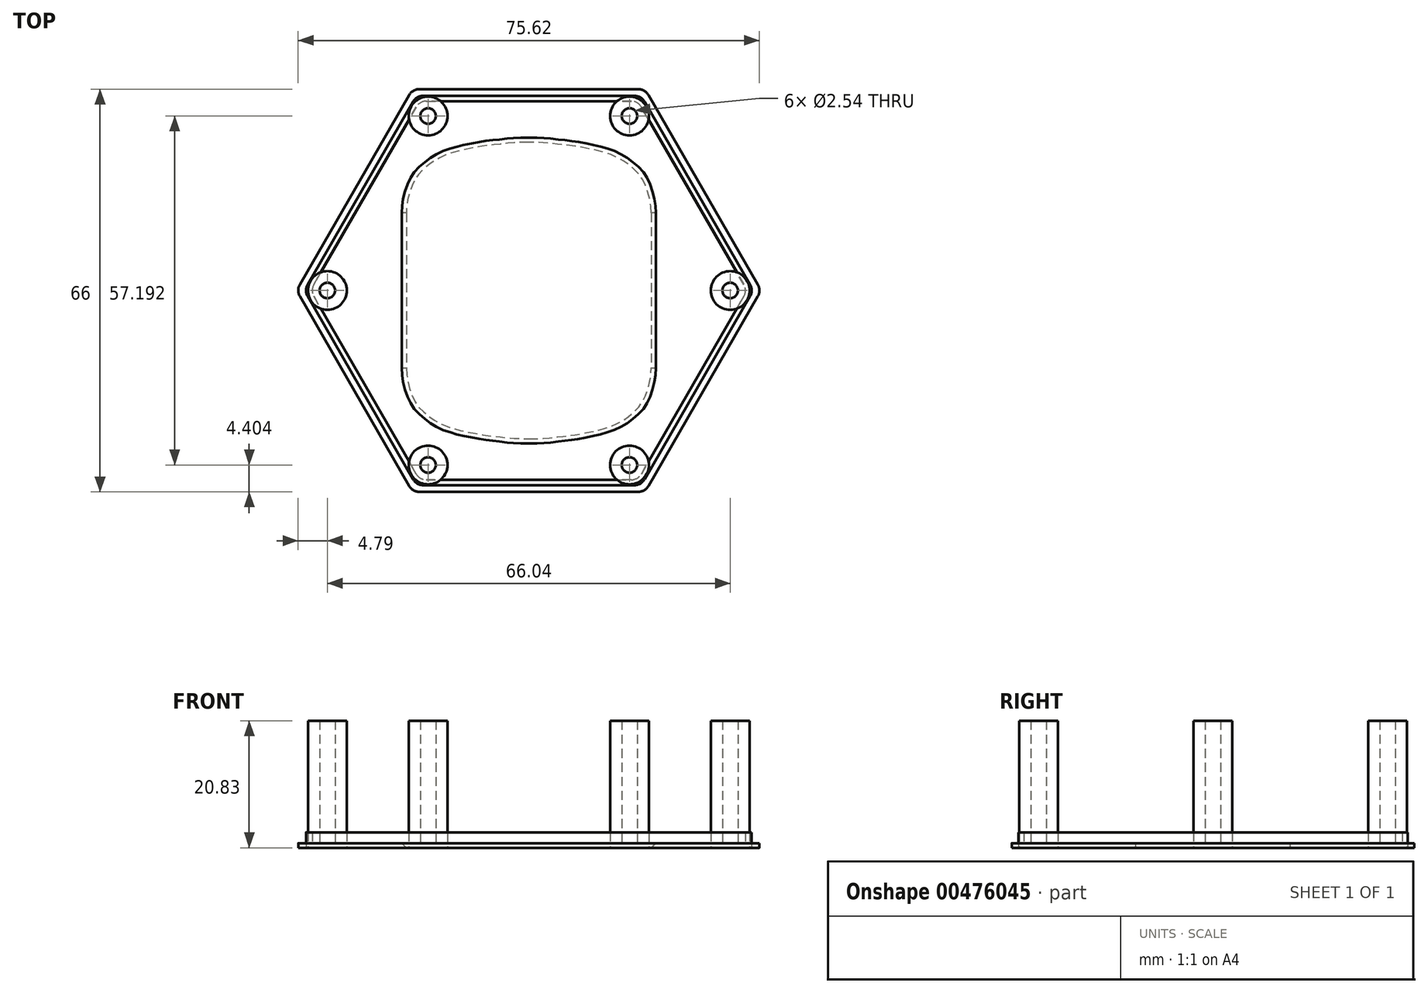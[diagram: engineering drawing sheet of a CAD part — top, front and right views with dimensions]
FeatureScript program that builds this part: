
annotation { "Feature Type Name" : "Feature", "Feature Type Description" : "" }
export const myFeature = defineFeature(function(context is Context, id is Id, definition is map)
    precondition{}
    {
        {
            var Q0;
            Q0=qCreatedBy(makeId("Top.planeOp"),FACE);
            var sketch = newSketch(context, id + "F0", { "sketchPlane" : qUnion([Q0])});
            skLineSegment(sketch, "E0", {"start": v(-56.1, -68.55) * mm, "end": v(58.07, -68.55) * mm});
            skLineSegment(sketch, "E1", {"start": v(0, 0) * mm, "end": v(-19.05, 33) * mm, "construction": true});
            skLineSegment(sketch, "E2", {"start": v(19.05, 33) * mm, "end": v(0, 0) * mm, "construction": true});
            skLineSegment(sketch, "E3", {"start": v(-19.05, 33) * mm, "end": v(19.05, 33) * mm});
            skLineSegment(sketch, "E4.1.0", {"start": v(-38.1, 0) * mm, "end": v(-19.05, 33) * mm});
            skLineSegment(sketch, "E4.2.0", {"start": v(-19.05, -33) * mm, "end": v(-38.1, 0) * mm});
            skLineSegment(sketch, "E4.3.0", {"start": v(19.05, -33) * mm, "end": v(-19.05, -33) * mm});
            skLineSegment(sketch, "E4.4.0", {"start": v(38.1, 0) * mm, "end": v(19.05, -33) * mm});
            skLineSegment(sketch, "E4.5.0", {"start": v(19.05, 33) * mm, "end": v(38.1, 0) * mm});
            skPoint(sketch, "E4.center", {"position": v(0, 0) * mm});
            skSolve(sketch);
        }
        {
            var Q0;
            Q0=makeQuery(id+"F0.imprint","IMPRINT",FACE,{"disambiguationData":[TD([[makeQuery(id+"F0.imprint","IMPRINT",EDGE,{"derivedFrom":sQuery(id+"F0.wireOp",EDGE,"E3")}),-1.0]])]});
            extrude(context, id + "F1", {"entities" : qUnion([Q0]), "depth" : 0.76 * mm, "offsetDistance" : 25.4 * mm});
        }
        {
            var Q0;
            Q0=makeQuery(id+"FdZoSmRdGPEDfu0_1.splitOp","SPLIT",EDGE,{"derivedFrom":makeQuery(id+"F1.opExtrude","SWEPT_EDGE",EDGE,{"disambiguationData":[OSD([sQuery(id+"F0.wireOp",EDGE,"E4.4.0"),sQuery(id+"F0.wireOp",EDGE,"E4.5.0")])]})});
            var Q1;
            Q1=makeQuery(id+"FdZoSmRdGPEDfu0_1.splitOp","SPLIT",EDGE,{"derivedFrom":makeQuery(id+"F1.opExtrude","SWEPT_EDGE",EDGE,{"disambiguationData":[OSD([sQuery(id+"F0.wireOp",EDGE,"E3"),sQuery(id+"F0.wireOp",EDGE,"E4.5.0")])]})});
            var Q2;
            Q2=makeQuery(id+"FdZoSmRdGPEDfu0_1.splitOp","SPLIT",EDGE,{"derivedFrom":makeQuery(id+"F1.opExtrude","SWEPT_EDGE",EDGE,{"disambiguationData":[OSD([sQuery(id+"F0.wireOp",EDGE,"E3"),sQuery(id+"F0.wireOp",EDGE,"E4.1.0")])]})});
            var Q3;
            Q3=makeQuery(id+"FdZoSmRdGPEDfu0_1.splitOp","SPLIT",EDGE,{"derivedFrom":makeQuery(id+"F1.opExtrude","SWEPT_EDGE",EDGE,{"disambiguationData":[OSD([sQuery(id+"F0.wireOp",EDGE,"E4.1.0"),sQuery(id+"F0.wireOp",EDGE,"E4.2.0")])]})});
            var Q4;
            Q4=makeQuery(id+"FdZoSmRdGPEDfu0_1.splitOp","SPLIT",EDGE,{"derivedFrom":makeQuery(id+"F1.opExtrude","SWEPT_EDGE",EDGE,{"disambiguationData":[OSD([sQuery(id+"F0.wireOp",EDGE,"E4.2.0"),sQuery(id+"F0.wireOp",EDGE,"E4.3.0")])]})});
            var Q5;
            Q5=makeQuery(id+"FdZoSmRdGPEDfu0_1.splitOp","SPLIT",EDGE,{"derivedFrom":makeQuery(id+"F1.opExtrude","SWEPT_EDGE",EDGE,{"disambiguationData":[OSD([sQuery(id+"F0.wireOp",EDGE,"E4.3.0"),sQuery(id+"F0.wireOp",EDGE,"E4.4.0")])]})});
            fillet(context, id + "F2", {"entities" : qUnion([Q0, Q1, Q2, Q3, Q4, Q5]), "radius" : 1.9 * mm, "allowEdgeOverflow" : false});
        }
        {
            var Q0;
            Q0=qCreatedBy(makeId("Top.planeOp"),FACE);
            var sketch = newSketch(context, id + "F3", { "sketchPlane" : qUnion([Q0])});
            skLineSegment(sketch, "E5", {"start": v(0, 0) * mm, "end": v(-18.41, 31.9) * mm, "construction": true});
            skLineSegment(sketch, "E6", {"start": v(0, 0) * mm, "end": v(18.41, 31.9) * mm, "construction": true});
            skLineSegment(sketch, "E7", {"start": v(-18.41, 31.9) * mm, "end": v(18.41, 31.9) * mm});
            skLineSegment(sketch, "E8.1.0", {"start": v(-36.83, 0) * mm, "end": v(-18.41, 31.9) * mm});
            skLineSegment(sketch, "E8.2.0", {"start": v(-18.42, -31.9) * mm, "end": v(-36.83, 0) * mm});
            skLineSegment(sketch, "E8.3.0", {"start": v(18.41, -31.9) * mm, "end": v(-18.41, -31.9) * mm});
            skLineSegment(sketch, "E8.4.0", {"start": v(36.83, 0) * mm, "end": v(18.41, -31.9) * mm});
            skLineSegment(sketch, "E8.5.0", {"start": v(18.41, 31.9) * mm, "end": v(36.83, 0) * mm});
            skPoint(sketch, "E8.center", {"position": v(0, 0) * mm});
            skSolve(sketch);
        }
        {
            var Q0;
            Q0=qSketchRegion(id+"F3",true);
            extrude(context, id + "F4", {"entities" : qUnion([Q0]), "depth" : 2.54 * mm, "offsetDistance" : 25.4 * mm});
        }
        {
            var Q0;
            Q0=makeQuery(id+"F4.opExtrude","SWEPT_EDGE",EDGE,{"disambiguationData":[OSD([sQuery(id+"F3.wireOp",EDGE,"E8.2.0"),sQuery(id+"F3.wireOp",EDGE,"E8.3.0")])]});
            var Q1;
            Q1=makeQuery(id+"F4.opExtrude","SWEPT_EDGE",EDGE,{"disambiguationData":[OSD([sQuery(id+"F3.wireOp",EDGE,"E8.3.0"),sQuery(id+"F3.wireOp",EDGE,"E8.4.0")])]});
            var Q2;
            Q2=makeQuery(id+"F4.opExtrude","SWEPT_EDGE",EDGE,{"disambiguationData":[OSD([sQuery(id+"F3.wireOp",EDGE,"E8.4.0"),sQuery(id+"F3.wireOp",EDGE,"E8.5.0")])]});
            var Q3;
            Q3=makeQuery(id+"F4.opExtrude","SWEPT_EDGE",EDGE,{"disambiguationData":[OSD([sQuery(id+"F3.wireOp",EDGE,"E8.1.0"),sQuery(id+"F3.wireOp",EDGE,"E8.2.0")])]});
            var Q4;
            Q4=makeQuery(id+"F4.opExtrude","SWEPT_EDGE",EDGE,{"disambiguationData":[OSD([sQuery(id+"F3.wireOp",EDGE,"E7"),sQuery(id+"F3.wireOp",EDGE,"E8.5.0")])]});
            var Q5;
            Q5=makeQuery(id+"F4.opExtrude","SWEPT_EDGE",EDGE,{"disambiguationData":[OSD([sQuery(id+"F3.wireOp",EDGE,"E7"),sQuery(id+"F3.wireOp",EDGE,"E8.1.0")])]});
            fillet(context, id + "F5", {"entities" : qUnion([Q0, Q1, Q2, Q3, Q4, Q5]), "radius" : 1.9 * mm, "tangentPropagation" : true, "allowEdgeOverflow" : false});
        }
        {
            var Q0;
            Q0=qCreatedBy(makeId("Top.planeOp"),FACE);
            var sketch = newSketch(context, id + "F6", { "sketchPlane" : qUnion([Q0])});
            skLineSegment(sketch, "E9", {"start": v(-17.9, 31.02) * mm, "end": v(0, 0) * mm, "construction": true});
            skLineSegment(sketch, "E10", {"start": v(0, 0) * mm, "end": v(17.9, 31.02) * mm, "construction": true});
            skLineSegment(sketch, "E11", {"start": v(-17.9, 31.02) * mm, "end": v(17.9, 31.02) * mm});
            skLineSegment(sketch, "E12.1.0", {"start": v(-35.81, 0) * mm, "end": v(-17.9, 31.02) * mm});
            skLineSegment(sketch, "E12.2.0", {"start": v(-17.9, -31.02) * mm, "end": v(-35.81, 0) * mm});
            skLineSegment(sketch, "E12.3.0", {"start": v(17.9, -31.02) * mm, "end": v(-17.9, -31.02) * mm});
            skLineSegment(sketch, "E12.4.0", {"start": v(35.81, 0) * mm, "end": v(17.9, -31.02) * mm});
            skLineSegment(sketch, "E12.5.0", {"start": v(17.9, 31.02) * mm, "end": v(35.81, 0) * mm});
            skPoint(sketch, "E12.center", {"position": v(0, 0) * mm});
            skSolve(sketch);
        }
        {
            var Q0;
            Q0=qSketchRegion(id+"F6",true);
            extrude(context, id + "F7", {"entities" : qUnion([Q0]), "depth" : 25.4 * mm, "offsetDistance" : 25.4 * mm});
        }
        {
            var Q0;
            Q0=makeQuery(id+"F7.opExtrude","SWEPT_EDGE",EDGE,{"disambiguationData":[OSD([sQuery(id+"F6.wireOp",EDGE,"E12.2.0"),sQuery(id+"F6.wireOp",EDGE,"E12.3.0")])]});
            var Q1;
            Q1=makeQuery(id+"F7.opExtrude","SWEPT_EDGE",EDGE,{"disambiguationData":[OSD([sQuery(id+"F6.wireOp",EDGE,"E12.3.0"),sQuery(id+"F6.wireOp",EDGE,"E12.4.0")])]});
            var Q2;
            Q2=makeQuery(id+"F7.opExtrude","SWEPT_EDGE",EDGE,{"disambiguationData":[OSD([sQuery(id+"F6.wireOp",EDGE,"E12.4.0"),sQuery(id+"F6.wireOp",EDGE,"E12.5.0")])]});
            var Q3;
            Q3=makeQuery(id+"F7.opExtrude","SWEPT_EDGE",EDGE,{"disambiguationData":[OSD([sQuery(id+"F6.wireOp",EDGE,"E12.1.0"),sQuery(id+"F6.wireOp",EDGE,"E12.2.0")])]});
            var Q4;
            Q4=makeQuery(id+"F7.opExtrude","SWEPT_EDGE",EDGE,{"disambiguationData":[OSD([sQuery(id+"F6.wireOp",EDGE,"E11"),sQuery(id+"F6.wireOp",EDGE,"E12.5.0")])]});
            var Q5;
            Q5=makeQuery(id+"F7.opExtrude","SWEPT_EDGE",EDGE,{"disambiguationData":[OSD([sQuery(id+"F6.wireOp",EDGE,"E11"),sQuery(id+"F6.wireOp",EDGE,"E12.1.0")])]});
            fillet(context, id + "F8", {"entities" : qUnion([Q0, Q1, Q2, Q3, Q4, Q5]), "radius" : 1.9 * mm, "tangentPropagation" : true, "allowEdgeOverflow" : false});
        }
        {
            var Q0;
            Q0=makeQuery(id+"F7.opExtrude","SWEPT_BODY",BODY,{"disambiguationData":[OSD([sQuery(id+"F6.wireOp",EDGE,"E11"),sQuery(id+"F6.wireOp",EDGE,"E12.1.0"),sQuery(id+"F6.wireOp",EDGE,"E12.2.0"),sQuery(id+"F6.wireOp",EDGE,"E12.3.0"),sQuery(id+"F6.wireOp",EDGE,"E12.4.0"),sQuery(id+"F6.wireOp",EDGE,"E12.5.0")])]});
            transform(context, id + "F9", {"entities" : qUnion([Q0]), "transformType" : TransformType.TRANSLATION_3D, "dx" : 0 * mm, "dy" : 0 * mm, "dz" : 0.76 * mm, "makeCopy" : false});
        }
        {
            var Q0;
            Q0=makeQuery(id+"F7.opExtrude","SWEPT_BODY",BODY,{"disambiguationData":[OSD([sQuery(id+"F6.wireOp",EDGE,"E11"),sQuery(id+"F6.wireOp",EDGE,"E12.1.0"),sQuery(id+"F6.wireOp",EDGE,"E12.2.0"),sQuery(id+"F6.wireOp",EDGE,"E12.3.0"),sQuery(id+"F6.wireOp",EDGE,"E12.4.0"),sQuery(id+"F6.wireOp",EDGE,"E12.5.0")])]});
            var Q1;
            Q1=makeQuery(id+"F4.opExtrude","SWEPT_BODY",BODY,{"disambiguationData":[OSD([sQuery(id+"F3.wireOp",EDGE,"E7"),sQuery(id+"F3.wireOp",EDGE,"E8.1.0"),sQuery(id+"F3.wireOp",EDGE,"E8.2.0"),sQuery(id+"F3.wireOp",EDGE,"E8.3.0"),sQuery(id+"F3.wireOp",EDGE,"E8.4.0"),sQuery(id+"F3.wireOp",EDGE,"E8.5.0")])]});
            booleanBodies(context, id + "F10", {"operationType" : BooleanOperationType.SUBTRACTION, "tools" : qUnion([Q0]), "targets" : qUnion([Q1])});
        }
        {
            var Q0;
            Q0=qCreatedBy(makeId("Right.planeOp"),FACE);
            var sketch = newSketch(context, id + "F11", { "sketchPlane" : qUnion([Q0])});
            skLineSegment(sketch, "E13", {"start": v(0, 0) * mm, "end": v(0, 42.96) * mm});
            skSolve(sketch);
        }
        {
            var Q0;
            Q0=qCreatedBy(makeId("Top.planeOp"),FACE);
            var sketch = newSketch(context, id + "F12", { "sketchPlane" : qUnion([Q0])});
            skLineSegment(sketch, "E14", {"start": v(-23.8, 19.58) * mm, "end": v(23.8, -19.58) * mm, "construction": true});
            skLineSegment(sketch, "E15", {"start": v(23.8, 19.58) * mm, "end": v(-23.8, -19.58) * mm, "construction": true});
            skPoint(sketch, "E16", {"position": v(0, 0) * mm});
            skLineSegment(sketch, "E17", {"start": v(0, 0) * mm, "end": v(-29.87, 10.71) * mm, "construction": true});
            skLineSegment(sketch, "E18", {"start": v(0, 0) * mm, "end": v(-10.76, 22.77) * mm, "construction": true});
            skLineSegment(sketch, "E19.MirrorCS", {"start": v(0, 0) * mm, "end": v(-29.87, -10.71) * mm, "construction": true});
            skLineSegment(sketch, "E20.MirrorCS", {"start": v(0, 0) * mm, "end": v(-10.76, -22.77) * mm, "construction": true});
            skPoint(sketch, "E21", {"position": v(-23.8, 0) * mm});
            skPoint(sketch, "E22", {"position": v(-12.7, -19.58) * mm});
            skPoint(sketch, "E23", {"position": v(-19.94, -16.4) * mm});
            skPoint(sketch, "E24", {"position": v(-23.01, -8.25) * mm});
            skPoint(sketch, "E25", {"position": v(-15.61, -19.14) * mm});
            skPoint(sketch, "E26", {"position": v(-17.79, -18.3) * mm});
            skPoint(sketch, "E27", {"position": v(-19.07, -17.4) * mm});
            skPoint(sketch, "E28", {"position": v(-16.47, -18.87) * mm});
            skPoint(sketch, "E29", {"position": v(-14.33, -19.44) * mm});
            skPoint(sketch, "E30", {"position": v(-23.47, -4.72) * mm});
            skPoint(sketch, "E31", {"position": v(-23.31, -6.36) * mm});
            skPoint(sketch, "E32", {"position": v(-22.01, -12.6) * mm});
            skPoint(sketch, "E33", {"position": v(-21.2, -14.53) * mm});
            skPoint(sketch, "E34", {"position": v(-22.6, -10.42) * mm});
            skPoint(sketch, "E35", {"position": v(-20.67, -15.48) * mm});
            skPoint(sketch, "E36", {"position": v(-21.7, -13.55) * mm});
            skPoint(sketch, "E37", {"position": v(-22.33, -11.55) * mm});
            skFitSpline(sketch, "E38", {"points": [v(-12.7, -19.58) * mm, v(-14.33, -19.44) * mm, v(-15.61, -19.14) * mm, v(-16.47, -18.87) * mm, v(-17.79, -18.3) * mm, v(-19.07, -17.4) * mm, v(-19.94, -16.4) * mm, v(-20.67, -15.48) * mm, v(-21.2, -14.53) * mm, v(-21.7, -13.55) * mm, v(-22.01, -12.6) * mm, v(-22.33, -11.55) * mm, v(-22.6, -10.42) * mm, v(-23.01, -8.25) * mm, v(-23.31, -6.36) * mm, v(-23.47, -4.72) * mm, v(-23.8, 0) * mm], "startDerivative": vector(-16.28, 0) * mm, "endDerivative": vector(0, 78.3) * mm});
            skFitSpline(sketch, "E39.MirrorCS", {"points": [v(-12.7, 19.58) * mm, v(-14.33, 19.44) * mm, v(-15.61, 19.14) * mm, v(-16.47, 18.87) * mm, v(-17.79, 18.3) * mm, v(-19.07, 17.4) * mm, v(-19.94, 16.4) * mm, v(-20.67, 15.48) * mm, v(-21.2, 14.53) * mm, v(-21.7, 13.55) * mm, v(-22.01, 12.6) * mm, v(-22.33, 11.55) * mm, v(-22.6, 10.42) * mm, v(-23.01, 8.25) * mm, v(-23.31, 6.36) * mm, v(-23.47, 4.72) * mm, v(-23.8, 0) * mm], "startDerivative": vector(-16.28, 0) * mm, "endDerivative": vector(0, -78.3) * mm});
            skFitSpline(sketch, "E40.MirrorCS", {"points": [v(12.7, -19.58) * mm, v(14.33, -19.44) * mm, v(15.61, -19.14) * mm, v(16.47, -18.87) * mm, v(17.79, -18.3) * mm, v(19.07, -17.4) * mm, v(19.94, -16.4) * mm, v(20.67, -15.48) * mm, v(21.2, -14.53) * mm, v(21.7, -13.55) * mm, v(22.01, -12.6) * mm, v(22.33, -11.55) * mm, v(22.6, -10.42) * mm, v(23.01, -8.25) * mm, v(23.31, -6.36) * mm, v(23.47, -4.72) * mm, v(23.8, 0) * mm], "startDerivative": vector(16.28, 0) * mm, "endDerivative": vector(0, 78.3) * mm});
            skFitSpline(sketch, "E41.MirrorCS", {"points": [v(12.7, 19.58) * mm, v(14.33, 19.44) * mm, v(15.61, 19.14) * mm, v(16.47, 18.87) * mm, v(17.79, 18.3) * mm, v(19.07, 17.4) * mm, v(19.94, 16.4) * mm, v(20.67, 15.48) * mm, v(21.2, 14.53) * mm, v(21.7, 13.55) * mm, v(22.01, 12.6) * mm, v(22.33, 11.55) * mm, v(22.6, 10.42) * mm, v(23.01, 8.25) * mm, v(23.31, 6.36) * mm, v(23.47, 4.72) * mm, v(23.8, 0) * mm], "startDerivative": vector(16.28, 0) * mm, "endDerivative": vector(0, -78.3) * mm});
            skLineSegment(sketch, "E42", {"start": v(-12.7, -19.58) * mm, "end": v(12.7, -19.58) * mm});
            skLineSegment(sketch, "E43", {"start": v(-12.7, 19.58) * mm, "end": v(12.7, 19.58) * mm});
            skSolve(sketch);
        }
        {
            var Q0;
            Q0 = qSketchRegion(id + "F12", true);
            extrude(context, id + "F13", {"entities" : qUnion([Q0]), "endBound" : BoundingType.SYMMETRIC, "depth" : 25.4 * mm, "offsetDistance" : 25.4 * mm});
        }
        {
            var Q0;
            Q0=makeQuery(id+"F13.opExtrude","SWEPT_BODY",BODY,{"disambiguationData":[OSD([sQuery(id+"F12.wireOp",EDGE,"E38"),sQuery(id+"F12.wireOp",EDGE,"E39.MirrorCS"),sQuery(id+"F12.wireOp",EDGE,"E40.MirrorCS"),sQuery(id+"F12.wireOp",EDGE,"E41.MirrorCS"),sQuery(id+"F12.wireOp",EDGE,"E42"),sQuery(id+"F12.wireOp",EDGE,"E43")])]});
            var Q1;
            Q1=sQuery(id+"F11.wireOp",EDGE,"E13");
            var Q2;
            Q2=sQuery(id+"F11.wireOp",EDGE,"E13");
            transform(context, id + "F14", {"entities" : qUnion([Q0]), "transformType" : TransformType.ROTATION, "transformAxis" : qUnion([Q2]), "angle" : 90 * degree, "makeCopy" : false});
        }
        {
            var Q0;
            Q0=makeQuery(id+"F13.opExtrude","SWEPT_BODY",BODY,{"disambiguationData":[OSD([sQuery(id+"F12.wireOp",EDGE,"E38"),sQuery(id+"F12.wireOp",EDGE,"E39.MirrorCS"),sQuery(id+"F12.wireOp",EDGE,"E40.MirrorCS"),sQuery(id+"F12.wireOp",EDGE,"E41.MirrorCS"),sQuery(id+"F12.wireOp",EDGE,"E42"),sQuery(id+"F12.wireOp",EDGE,"E43")])]});
            var Q1;
            Q1=makeQuery(id+"F4.opExtrude","SWEPT_BODY",BODY,{"disambiguationData":[OSD([sQuery(id+"F3.wireOp",EDGE,"E7"),sQuery(id+"F3.wireOp",EDGE,"E8.1.0"),sQuery(id+"F3.wireOp",EDGE,"E8.2.0"),sQuery(id+"F3.wireOp",EDGE,"E8.3.0"),sQuery(id+"F3.wireOp",EDGE,"E8.4.0"),sQuery(id+"F3.wireOp",EDGE,"E8.5.0")])]});
            booleanBodies(context, id + "F15", {"operationType" : BooleanOperationType.SUBTRACTION, "tools" : qUnion([Q0]), "targets" : qUnion([Q1])});
        }
        {
            var Q0;
            Q0=makeQuery(id+"F15.opBoolean","INTERSECT",EDGE,{"derivedFrom":[makeQuery(id+"F10.opBoolean","COPY",FACE,{"derivedFrom":makeQuery(id+"F7.opExtrude","CAP_FACE",FACE,{"disambiguationData":[OSD([sQuery(id+"F6.wireOp",EDGE,"E11"),sQuery(id+"F6.wireOp",EDGE,"E12.1.0"),sQuery(id+"F6.wireOp",EDGE,"E12.2.0"),sQuery(id+"F6.wireOp",EDGE,"E12.3.0"),sQuery(id+"F6.wireOp",EDGE,"E12.4.0"),sQuery(id+"F6.wireOp",EDGE,"E12.5.0")])],"isStart":true})}),makeQuery(id+"F13.opExtrude","SWEPT_FACE",FACE,{"disambiguationData":[OSD([sQuery(id+"F12.wireOp",EDGE,"E38")])]})]});
            var Q1;
            Q1=makeQuery(id+"F15.opBoolean","INTERSECT",EDGE,{"derivedFrom":[makeQuery(id+"F10.opBoolean","COPY",FACE,{"derivedFrom":makeQuery(id+"F7.opExtrude","CAP_FACE",FACE,{"disambiguationData":[OSD([sQuery(id+"F6.wireOp",EDGE,"E11"),sQuery(id+"F6.wireOp",EDGE,"E12.1.0"),sQuery(id+"F6.wireOp",EDGE,"E12.2.0"),sQuery(id+"F6.wireOp",EDGE,"E12.3.0"),sQuery(id+"F6.wireOp",EDGE,"E12.4.0"),sQuery(id+"F6.wireOp",EDGE,"E12.5.0")])],"isStart":true})}),makeQuery(id+"F13.opExtrude","SWEPT_FACE",FACE,{"disambiguationData":[OSD([sQuery(id+"F12.wireOp",EDGE,"E39.MirrorCS")])]})]});
            var Q2;
            Q2=makeQuery(id+"F15.opBoolean","INTERSECT",EDGE,{"derivedFrom":[makeQuery(id+"F10.opBoolean","COPY",FACE,{"derivedFrom":makeQuery(id+"F7.opExtrude","CAP_FACE",FACE,{"disambiguationData":[OSD([sQuery(id+"F6.wireOp",EDGE,"E11"),sQuery(id+"F6.wireOp",EDGE,"E12.1.0"),sQuery(id+"F6.wireOp",EDGE,"E12.2.0"),sQuery(id+"F6.wireOp",EDGE,"E12.3.0"),sQuery(id+"F6.wireOp",EDGE,"E12.4.0"),sQuery(id+"F6.wireOp",EDGE,"E12.5.0")])],"isStart":true})}),makeQuery(id+"F13.opExtrude","SWEPT_FACE",FACE,{"disambiguationData":[OSD([sQuery(id+"F12.wireOp",EDGE,"E43")])]})]});
            var Q3;
            Q3=makeQuery(id+"F15.opBoolean","INTERSECT",EDGE,{"derivedFrom":[makeQuery(id+"F10.opBoolean","COPY",FACE,{"derivedFrom":makeQuery(id+"F7.opExtrude","CAP_FACE",FACE,{"disambiguationData":[OSD([sQuery(id+"F6.wireOp",EDGE,"E11"),sQuery(id+"F6.wireOp",EDGE,"E12.1.0"),sQuery(id+"F6.wireOp",EDGE,"E12.2.0"),sQuery(id+"F6.wireOp",EDGE,"E12.3.0"),sQuery(id+"F6.wireOp",EDGE,"E12.4.0"),sQuery(id+"F6.wireOp",EDGE,"E12.5.0")])],"isStart":true})}),makeQuery(id+"F13.opExtrude","SWEPT_FACE",FACE,{"disambiguationData":[OSD([sQuery(id+"F12.wireOp",EDGE,"E41.MirrorCS")])]})]});
            var Q4;
            Q4=makeQuery(id+"F15.opBoolean","INTERSECT",EDGE,{"derivedFrom":[makeQuery(id+"F10.opBoolean","COPY",FACE,{"derivedFrom":makeQuery(id+"F7.opExtrude","CAP_FACE",FACE,{"disambiguationData":[OSD([sQuery(id+"F6.wireOp",EDGE,"E11"),sQuery(id+"F6.wireOp",EDGE,"E12.1.0"),sQuery(id+"F6.wireOp",EDGE,"E12.2.0"),sQuery(id+"F6.wireOp",EDGE,"E12.3.0"),sQuery(id+"F6.wireOp",EDGE,"E12.4.0"),sQuery(id+"F6.wireOp",EDGE,"E12.5.0")])],"isStart":true})}),makeQuery(id+"F13.opExtrude","SWEPT_FACE",FACE,{"disambiguationData":[OSD([sQuery(id+"F12.wireOp",EDGE,"E40.MirrorCS")])]})]});
            var Q5;
            Q5=makeQuery(id+"F15.opBoolean","INTERSECT",EDGE,{"derivedFrom":[makeQuery(id+"F10.opBoolean","COPY",FACE,{"derivedFrom":makeQuery(id+"F7.opExtrude","CAP_FACE",FACE,{"disambiguationData":[OSD([sQuery(id+"F6.wireOp",EDGE,"E11"),sQuery(id+"F6.wireOp",EDGE,"E12.1.0"),sQuery(id+"F6.wireOp",EDGE,"E12.2.0"),sQuery(id+"F6.wireOp",EDGE,"E12.3.0"),sQuery(id+"F6.wireOp",EDGE,"E12.4.0"),sQuery(id+"F6.wireOp",EDGE,"E12.5.0")])],"isStart":true})}),makeQuery(id+"F13.opExtrude","SWEPT_FACE",FACE,{"disambiguationData":[OSD([sQuery(id+"F12.wireOp",EDGE,"E42")])]})]});
            chamfer(context, id + "F16", {"entities" : qUnion([Q0, Q1, Q2, Q3, Q4, Q5]), "width" : 1.27 * mm});
        }
        {
            var Q0;
            Q0=qCreatedBy(makeId("Top.planeOp"),FACE);
            var sketch = newSketch(context, id + "F17", { "sketchPlane" : qUnion([Q0])});
            skLineSegment(sketch, "E44", {"start": v(0, 0) * mm, "end": v(-30.37, 52.6) * mm, "construction": true});
            skLineSegment(sketch, "E45", {"start": v(0, 0) * mm, "end": v(28.61, 49.56) * mm, "construction": true});
            skPoint(sketch, "E46", {"position": v(-16.51, 28.6) * mm});
            skCircle(sketch, "E47", {"center": v(-16.51, 28.6) * mm, "radius": 3.18 * mm});
            skCircle(sketch, "E48", {"center": v(-16.51, 28.6) * mm, "radius": 1.27 * mm});
            skCircle(sketch, "E49.1.0", {"center": v(-33.02, 0) * mm, "radius": 3.18 * mm});
            skCircle(sketch, "E49.1.1", {"center": v(-33.02, 0) * mm, "radius": 1.27 * mm});
            skCircle(sketch, "E49.2.0", {"center": v(-16.51, -28.6) * mm, "radius": 3.18 * mm});
            skCircle(sketch, "E49.2.1", {"center": v(-16.51, -28.6) * mm, "radius": 1.27 * mm});
            skCircle(sketch, "E49.3.0", {"center": v(16.5, -28.6) * mm, "radius": 3.18 * mm});
            skCircle(sketch, "E49.3.1", {"center": v(16.5, -28.6) * mm, "radius": 1.27 * mm});
            skCircle(sketch, "E49.4.0", {"center": v(33.02, 0) * mm, "radius": 3.18 * mm});
            skCircle(sketch, "E49.4.1", {"center": v(33.02, 0) * mm, "radius": 1.27 * mm});
            skCircle(sketch, "E49.5.0", {"center": v(16.51, 28.6) * mm, "radius": 3.18 * mm});
            skCircle(sketch, "E49.5.1", {"center": v(16.51, 28.6) * mm, "radius": 1.27 * mm});
            skPoint(sketch, "E49.center", {"position": v(0, 0) * mm});
            skSolve(sketch);
        }
        {
            var Q0;
            Q0=makeQuery(id+"F17.imprint","IMPRINT",FACE,{"disambiguationData":[TD([[makeQuery(id+"F17.imprint","IMPRINT",EDGE,{"derivedFrom":sQuery(id+"F17.wireOp",EDGE,"E47")}),1.0]])]});
            var Q1;
            Q1=makeQuery(id+"F17.imprint","IMPRINT",FACE,{"disambiguationData":[TD([[makeQuery(id+"F17.imprint","IMPRINT",EDGE,{"derivedFrom":sQuery(id+"F17.wireOp",EDGE,"E49.1.0")}),1.0]])]});
            var Q2;
            Q2=makeQuery(id+"F17.imprint","IMPRINT",FACE,{"disambiguationData":[TD([[makeQuery(id+"F17.imprint","IMPRINT",EDGE,{"derivedFrom":sQuery(id+"F17.wireOp",EDGE,"E49.2.0")}),1.0]])]});
            var Q3;
            Q3=makeQuery(id+"F17.imprint","IMPRINT",FACE,{"disambiguationData":[TD([[makeQuery(id+"F17.imprint","IMPRINT",EDGE,{"derivedFrom":sQuery(id+"F17.wireOp",EDGE,"E49.3.0")}),1.0]])]});
            var Q4;
            Q4=makeQuery(id+"F17.imprint","IMPRINT",FACE,{"disambiguationData":[TD([[makeQuery(id+"F17.imprint","IMPRINT",EDGE,{"derivedFrom":sQuery(id+"F17.wireOp",EDGE,"E49.4.0")}),1.0]])]});
            var Q5;
            Q5=makeQuery(id+"F17.imprint","IMPRINT",FACE,{"disambiguationData":[TD([[makeQuery(id+"F17.imprint","IMPRINT",EDGE,{"derivedFrom":sQuery(id+"F17.wireOp",EDGE,"E49.5.0")}),1.0]])]});
            var Q6;
            Q6=sQuery(id+"F17.wireOp",EDGE,"E47");
            extrude(context, id + "F18", {"entities" : qUnion([Q0, Q1, Q2, Q3, Q4, Q5]), "surfaceEntities" : qUnion([Q6]), "depth" : 20.83 * mm, "offsetDistance" : 25.4 * mm});
        }
    });
